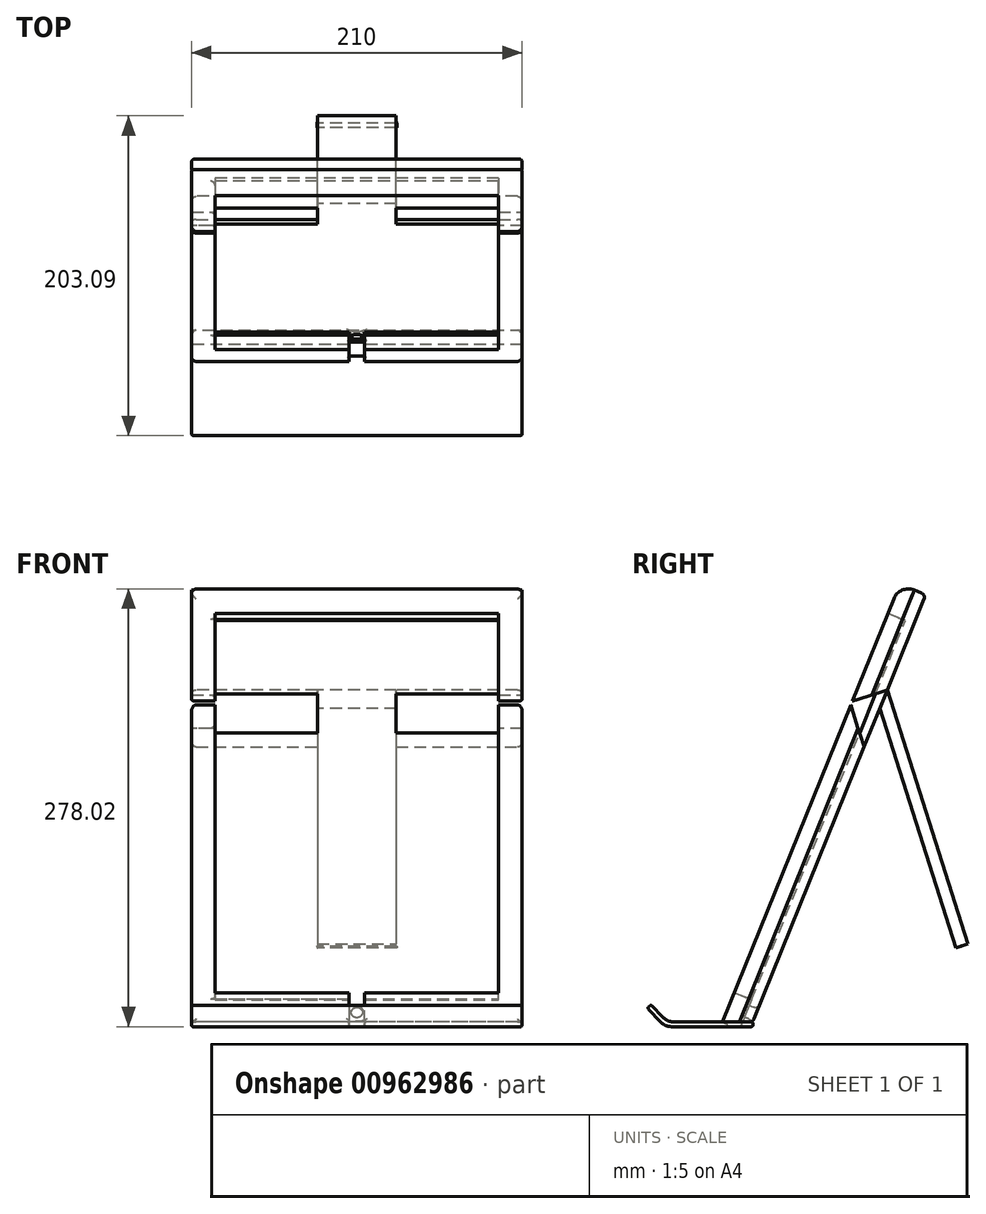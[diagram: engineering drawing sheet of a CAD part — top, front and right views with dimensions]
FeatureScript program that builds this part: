
annotation { "Feature Type Name" : "Feature", "Feature Type Description" : "" }
export const myFeature = defineFeature(function(context is Context, id is Id, definition is map)
    precondition{}
    {
        {
            var Q0;
            Q0=qCreatedBy(makeId("Right.planeOp"),FACE);
            var sketch = newSketch(context, id + "F0", { "sketchPlane" : qUnion([Q0])});
            skLineSegment(sketch, "E0", {"start": v(10.79, 0) * mm, "end": v(121.93, 274.29) * mm});
            skLineSegment(sketch, "E1", {"start": v(121.93, 274.29) * mm, "end": v(112.66, 278.04) * mm});
            skLineSegment(sketch, "E2", {"start": v(112.66, 278.04) * mm, "end": v(0, 0) * mm});
            skLineSegment(sketch, "E3", {"start": v(0, 0) * mm, "end": v(10.79, 0) * mm});
            skSolve(sketch);
        }
        {
            var Q0;
            Q0 = qSketchRegion(id + "F0", true);
            extrude(context, id + "F1", {"entities" : qUnion([Q0]), "depth" : 210 * mm, "offsetDistance" : 25 * mm});
        }
        {
            var Q0;
            Q0=qCreatedBy(makeId("Right.planeOp"),FACE);
            var sketch = newSketch(context, id + "F2", { "sketchPlane" : qUnion([Q0])});
            skLineSegment(sketch, "E4.0", {"start": v(10.79, 0) * mm, "end": v(121.93, 274.29) * mm});
            skLineSegment(sketch, "E5", {"start": v(121.93, 274.29) * mm, "end": v(129.34, 271.28) * mm});
            skLineSegment(sketch, "E6", {"start": v(129.34, 271.28) * mm, "end": v(19.42, 0) * mm});
            skLineSegment(sketch, "E7", {"start": v(19.42, 0) * mm, "end": v(10.79, 0) * mm});
            skSolve(sketch);
        }
        {
            var Q0;
            Q0 = qSketchRegion(id + "F2", true);
            extrude(context, id + "F3", {"entities" : qUnion([Q0]), "depth" : 210 * mm, "offsetDistance" : 25 * mm});
        }
        {
            var Q0;
            Q0=makeQuery(id+"F1.opExtrude","SWEPT_EDGE",EDGE,{"disambiguationData":[OSD([sQuery(id+"F0.wireOp",EDGE,"E1"),sQuery(id+"F0.wireOp",EDGE,"E2")])]});
            fillet(context, id + "F4", {"entities" : qUnion([Q0]), "radius" : 10 * mm, "tangentPropagation" : true, "allowEdgeOverflow" : false});
        }
        {
            var Q0;
            Q0=qCreatedBy(makeId("Right.planeOp"),FACE);
            var sketch = newSketch(context, id + "F5", { "sketchPlane" : qUnion([Q0])});
            skLineSegment(sketch, "E8.0", {"start": v(0, 0) * mm, "end": v(10.79, 0) * mm});
            skLineSegment(sketch, "E9.0", {"start": v(19.42, 0) * mm, "end": v(10.79, 0) * mm});
            skLineSegment(sketch, "E10", {"start": v(19.42, 0) * mm, "end": v(19.42, -3) * mm});
            skLineSegment(sketch, "E11", {"start": v(0, 0) * mm, "end": v(-35, 0) * mm});
            skLineSegment(sketch, "E12", {"start": v(-35, 0) * mm, "end": v(-45.29, 10.92) * mm});
            skLineSegment(sketch, "E13", {"start": v(-45.29, 10.92) * mm, "end": v(-47.47, 8.86) * mm});
            skLineSegment(sketch, "E14", {"start": v(-47.47, 8.86) * mm, "end": v(-36.3, -3) * mm});
            skLineSegment(sketch, "E15", {"start": v(19.42, -3) * mm, "end": v(-36.3, -3) * mm});
            skSolve(sketch);
        }
        {
            var Q0;
            Q0=makeQuery(id+"F1.opExtrude","SWEPT_FACE",FACE,{"disambiguationData":[OSD([sQuery(id+"F0.wireOp",EDGE,"E2")])]});
            var sketch = newSketch(context, id + "F6", { "sketchPlane" : qUnion([Q0])});
            skLineSegment(sketch, "E16", {"start": v(15, 20) * mm, "end": v(100, 20) * mm});
            skLineSegment(sketch, "E17", {"start": v(195, 20) * mm, "end": v(195, 280) * mm});
            skLineSegment(sketch, "E18", {"start": v(195, 280) * mm, "end": v(15, 280) * mm});
            skLineSegment(sketch, "E19", {"start": v(15, 280) * mm, "end": v(15, 20) * mm});
            skLineSegment(sketch, "E20", {"start": v(105, 0) * mm, "end": v(110, 0) * mm});
            skLineSegment(sketch, "E21", {"start": v(110, 0) * mm, "end": v(110, 20) * mm});
            skLineSegment(sketch, "E22", {"start": v(100, 20) * mm, "end": v(100, 0) * mm});
            skLineSegment(sketch, "E23", {"start": v(100, 0) * mm, "end": v(105, 0) * mm});
            skLineSegment(sketch, "E24.trimOffspring", {"start": v(110, 20) * mm, "end": v(195, 20) * mm});
            skSolve(sketch);
        }
        {
            var Q0;
            Q0 = qSketchRegion(id + "F5", true);
            extrude(context, id + "F7", {"entities" : qUnion([Q0]), "depth" : 210 * mm, "offsetDistance" : 25 * mm});
        }
        {
            var Q0;
            Q0 = qSketchRegion(id + "F6", true);
            extrude(context, id + "F8", {"entities" : qUnion([Q0]), "operationType" : NewBodyOperationType.REMOVE, "oppositeDirection" : true, "depth" : 12 * mm, "offsetDistance" : 25 * mm});
        }
        {
            var Q0;
            Q0=makeQuery(id+"F3.opExtrude","SWEPT_FACE",FACE,{"disambiguationData":[OSD([sQuery(id+"F2.wireOp",EDGE,"E4.0")])]});
            var sketch = newSketch(context, id + "F9", { "sketchPlane" : qUnion([Q0])});
            skCircle(sketch, "E25", {"center": v(105, 12.05) * mm, "radius": 4 * mm});
            skLineSegment(sketch, "E26", {"start": v(105, 4.05) * mm, "end": v(105, 12.05) * mm, "construction": true});
            skSolve(sketch);
        }
        {
            var Q0;
            Q0 = qSketchRegion(id + "F9", true);
            extrude(context, id + "F10", {"entities" : qUnion([Q0]), "operationType" : NewBodyOperationType.REMOVE, "oppositeDirection" : true, "depth" : 25 * mm, "offsetDistance" : 25 * mm});
        }
        {
            var Q0;
            Q0=makeQuery(id+"F1.opExtrude","CAP_EDGE",EDGE,{"disambiguationData":[OSD([sQuery(id+"F0.wireOp",EDGE,"E2")])],"isStart":false});
            var Q1;
            Q1=makeQuery(id+"F1.opExtrude","CAP_EDGE",EDGE,{"disambiguationData":[OSD([sQuery(id+"F0.wireOp",EDGE,"E2")])],"isStart":true});
            var Q2;
            Q2=makeQuery(id+"F3.opExtrude","SWEPT_FACE",FACE,{"disambiguationData":[OSD([sQuery(id+"F2.wireOp",EDGE,"E6")])]});
            var Q3;
            Q3=makeQuery(id+"F8.boolean.opBoolean","COPY",EDGE,{"derivedFrom":makeQuery(id+"F8.opExtrude","CAP_EDGE",EDGE,{"disambiguationData":[OSD([sQuery(id+"F6.wireOp",EDGE,"E16")])],"isStart":true})});
            var Q4;
            Q4=makeQuery(id+"F8.boolean.opBoolean","INTERSECT",EDGE,{"derivedFrom":[makeQuery(id+"F1.opExtrude","SWEPT_FACE",FACE,{"disambiguationData":[OSD([sQuery(id+"F0.wireOp",EDGE,"E0")])]}),makeQuery(id+"F8.opExtrude","SWEPT_FACE",FACE,{"disambiguationData":[OSD([sQuery(id+"F6.wireOp",EDGE,"E19")])]})]});
            var Q5;
            Q5=makeQuery(id+"F8.boolean.opBoolean","COPY",EDGE,{"derivedFrom":makeQuery(id+"F8.opExtrude","CAP_EDGE",EDGE,{"disambiguationData":[OSD([sQuery(id+"F6.wireOp",EDGE,"E17")])],"isStart":true})});
            var Q6;
            Q6=makeQuery(id+"F8.boolean.opBoolean","COPY",EDGE,{"derivedFrom":makeQuery(id+"F8.opExtrude","CAP_EDGE",EDGE,{"disambiguationData":[OSD([sQuery(id+"F6.wireOp",EDGE,"E24.trimOffspring")])],"isStart":true})});
            var Q7;
            Q7=makeQuery(id+"F8.boolean.opBoolean","COPY",EDGE,{"derivedFrom":makeQuery(id+"F8.opExtrude","CAP_EDGE",EDGE,{"disambiguationData":[OSD([sQuery(id+"F6.wireOp",EDGE,"E19")])],"isStart":true})});
            var Q8;
            Q8=makeQuery(id+"F8.boolean.opBoolean","COPY",EDGE,{"derivedFrom":makeQuery(id+"F8.opExtrude","CAP_EDGE",EDGE,{"disambiguationData":[OSD([sQuery(id+"F6.wireOp",EDGE,"E21")])],"isStart":true})});
            var Q9;
            Q9=makeQuery(id+"F8.boolean.opBoolean","COPY",EDGE,{"derivedFrom":makeQuery(id+"F8.opExtrude","CAP_EDGE",EDGE,{"disambiguationData":[OSD([sQuery(id+"F6.wireOp",EDGE,"E22")])],"isStart":true})});
            var Q10;
            Q10=makeQuery(id+"F8.boolean.opBoolean","COPY",EDGE,{"derivedFrom":makeQuery(id+"F8.opExtrude","CAP_EDGE",EDGE,{"disambiguationData":[OSD([sQuery(id+"F6.wireOp",EDGE,"E18")])],"isStart":true})});
            fillet(context, id + "F11", {"entities" : qUnion([Q0, Q1, Q2, Q3, Q4, Q5, Q6, Q7, Q8, Q9, Q10]), "radius" : 3 * mm, "tangentPropagation" : true, "allowEdgeOverflow" : false});
        }
        {
            var Q0;
            Q0=qCreatedBy(makeId("Right.planeOp"),FACE);
            var sketch = newSketch(context, id + "F12", { "sketchPlane" : qUnion([Q0])});
            skLineSegment(sketch, "E27.0", {"start": v(128.22, 268.5) * mm, "end": v(20.18, 1.87) * mm});
            skLineSegment(sketch, "E28", {"start": v(100.14, 199.2) * mm, "end": v(163.38, 0) * mm});
            skLineSegment(sketch, "E29", {"start": v(163.38, 0) * mm, "end": v(171, 2.42) * mm});
            skLineSegment(sketch, "E30", {"start": v(171, 2.42) * mm, "end": v(104.84, 210.82) * mm});
            skSolve(sketch);
        }
        {
            var Q0;
            Q0 = qSketchRegion(id + "F12", true);
            extrude(context, id + "F13", {"entities" : qUnion([Q0]), "depth" : 210 * mm, "offsetDistance" : 25 * mm});
        }
        {
            var Q0;
            Q0=makeQuery(id+"F13.opExtrude","SWEPT_FACE",FACE,{"disambiguationData":[OSD([sQuery(id+"F12.wireOp",EDGE,"E30")])]});
            var sketch = newSketch(context, id + "F14", { "sketchPlane" : qUnion([Q0])});
            skLineSegment(sketch, "E31", {"start": v(-105, -49.44) * mm, "end": v(-105, 239.2) * mm, "construction": true});
            skLineSegment(sketch, "E32", {"start": v(-190, -20) * mm, "end": v(-210, -49.44) * mm});
            skLineSegment(sketch, "E33", {"start": v(-20, -20) * mm, "end": v(0, -49.44) * mm});
            skPoint(sketch, "E34.orphan", {"position": v(0, -19.85) * mm});
            skLineSegment(sketch, "E35", {"start": v(-210, -49.44) * mm, "end": v(-210, 169.2) * mm});
            skLineSegment(sketch, "E36", {"start": v(-210, 169.2) * mm, "end": v(-130, 169.2) * mm});
            skLineSegment(sketch, "E37", {"start": v(-80, 169.2) * mm, "end": v(0, 169.2) * mm});
            skLineSegment(sketch, "E38", {"start": v(0, 169.2) * mm, "end": v(0, -49.44) * mm});
            skLineSegment(sketch, "E39", {"start": v(0, -49.44) * mm, "end": v(-20, -20) * mm});
            skPoint(sketch, "E40.start.orphan", {"position": v(-105, 169.2) * mm});
            skPoint(sketch, "E41.end.orphan", {"position": v(-130, 0) * mm});
            skPoint(sketch, "E42.end.orphan", {"position": v(-80.13, 0) * mm});
            skLineSegment(sketch, "E43", {"start": v(-80, 169.2) * mm, "end": v(-80, -0.8) * mm});
            skLineSegment(sketch, "E44", {"start": v(-80, -0.8) * mm, "end": v(-80, 169.2) * mm});
            skLineSegment(sketch, "E45", {"start": v(-130, 169.2) * mm, "end": v(-130, -0.8) * mm});
            skLineSegment(sketch, "E46", {"start": v(-80, -0.8) * mm, "end": v(-20, -20) * mm});
            skLineSegment(sketch, "E47", {"start": v(-20, -20) * mm, "end": v(0, -20) * mm});
            skLineSegment(sketch, "E48", {"start": v(-130, 169.2) * mm, "end": v(-80, 169.2) * mm});
            skLineSegment(sketch, "E49", {"start": v(-190, -20) * mm, "end": v(-210, -20) * mm});
            skLineSegment(sketch, "E50", {"start": v(-130, -0.8) * mm, "end": v(-190, -20) * mm});
            skSolve(sketch);
        }
        {
            var Q0;
            Q0 = qSketchRegion(id + "F14", true);
            extrude(context, id + "F15", {"entities" : qUnion([Q0]), "operationType" : NewBodyOperationType.REMOVE, "oppositeDirection" : true, "depth" : 25 * mm, "offsetDistance" : 25 * mm});
        }
        {
            var Q0;
            Q0=makeQuery(id+"F15.boolean.opBoolean","COPY",EDGE,{"derivedFrom":makeQuery(id+"F15.opExtrude","CAP_EDGE",EDGE,{"disambiguationData":[OSD([sQuery(id+"F14.wireOp",EDGE,"E42")])],"isStart":true})});
            var Q1;
            Q1=makeQuery(id+"F15.boolean.opBoolean","COPY",EDGE,{"derivedFrom":makeQuery(id+"F15.opExtrude","CAP_EDGE",EDGE,{"disambiguationData":[OSD([sQuery(id+"F14.wireOp",EDGE,"E41")])],"isStart":true})});
            var Q2;
            Q2=makeQuery(id+"F15.boolean.opBoolean","COPY",EDGE,{"derivedFrom":makeQuery(id+"F15.opExtrude","CAP_EDGE",EDGE,{"disambiguationData":[OSD([sQuery(id+"F14.wireOp",EDGE,"zWq83p2V-2280-gHE3-ipJg-bSoWOM0zsTTD")])],"isStart":true})});
            var Q3;
            Q3=makeQuery(id+"F15.boolean.opBoolean","COPY",EDGE,{"derivedFrom":makeQuery(id+"F15.opExtrude","CAP_EDGE",EDGE,{"disambiguationData":[OSD([sQuery(id+"F14.wireOp",EDGE,"E32")])],"isStart":true})});
            var Q4;
            Q4=makeQuery(id+"F13.opExtrude","SWEPT_EDGE",EDGE,{"disambiguationData":[OSD([sQuery(id+"F12.wireOp",EDGE,"E29"),sQuery(id+"F12.wireOp",EDGE,"E30")])]});
            var Q5;
            Q5=makeQuery(id+"F15.boolean.opBoolean","COPY",EDGE,{"derivedFrom":makeQuery(id+"F15.opExtrude","CAP_EDGE",EDGE,{"disambiguationData":[OSD([sQuery(id+"F14.wireOp",EDGE,"E39")])],"isStart":true})});
            var Q6;
            Q6=makeQuery(id+"F15.boolean.opBoolean","COPY",EDGE,{"derivedFrom":makeQuery(id+"F15.opExtrude","CAP_EDGE",EDGE,{"disambiguationData":[OSD([sQuery(id+"F14.wireOp",EDGE,"iIxzz1AC-Ownc-jVEO-BnMf-pMrgPYKgyDFp")])],"isStart":true})});
            var Q7;
            Q7=makeQuery(id+"F15.boolean.opBoolean","COPY",EDGE,{"derivedFrom":makeQuery(id+"F15.opExtrude","CAP_EDGE",EDGE,{"disambiguationData":[OSD([sQuery(id+"F14.wireOp",EDGE,"E50")])],"isStart":true})});
            var Q8;
            Q8=makeQuery(id+"F15.boolean.opBoolean","COPY",EDGE,{"derivedFrom":makeQuery(id+"F15.opExtrude","CAP_EDGE",EDGE,{"disambiguationData":[OSD([sQuery(id+"F14.wireOp",EDGE,"E46")])],"isStart":true})});
            var Q9;
            Q9=makeQuery(id+"F15.boolean.opBoolean","COPY",EDGE,{"derivedFrom":makeQuery(id+"F15.opExtrude","CAP_EDGE",EDGE,{"disambiguationData":[OSD([sQuery(id+"F14.wireOp",EDGE,"E44")])],"isStart":true})});
            var Q10;
            Q10=makeQuery(id+"F15.boolean.opBoolean","COPY",EDGE,{"derivedFrom":makeQuery(id+"F15.opExtrude","CAP_EDGE",EDGE,{"disambiguationData":[OSD([sQuery(id+"F14.wireOp",EDGE,"E45")])],"isStart":true})});
            fillet(context, id + "F16", {"entities" : qUnion([Q0, Q1, Q2, Q3, Q4, Q5, Q6, Q7, Q8, Q9, Q10]), "radius" : 5 * mm, "tangentPropagation" : true, "allowEdgeOverflow" : false});
        }
        {
            var Q0;
            Q0=makeQuery(id+"F7.opExtrude","SWEPT_EDGE",EDGE,{"disambiguationData":[OSD([sQuery(id+"F5.wireOp",EDGE,"E11"),sQuery(id+"F5.wireOp",EDGE,"E12")])]});
            var Q1;
            Q1=makeQuery(id+"F7.opExtrude","SWEPT_EDGE",EDGE,{"disambiguationData":[OSD([sQuery(id+"F5.wireOp",EDGE,"E14"),sQuery(id+"F5.wireOp",EDGE,"E15")])]});
            fillet(context, id + "F17", {"entities" : qUnion([Q0, Q1]), "radius" : 10 * mm, "tangentPropagation" : true, "allowEdgeOverflow" : false});
        }
        {
            var Q0;
            Q0=makeQuery(id+"F7.opExtrude","SWEPT_FACE",FACE,{"disambiguationData":[OSD([sQuery(id+"F5.wireOp",EDGE,"E8.0"),sQuery(id+"F5.wireOp",EDGE,"E9.0"),sQuery(id+"F5.wireOp",EDGE,"E11")])]});
            var Q1;
            Q1=makeQuery(id+"F7.opExtrude","SWEPT_FACE",FACE,{"disambiguationData":[OSD([sQuery(id+"F5.wireOp",EDGE,"E15")])]});
            var Q2;
            Q2=makeQuery(id+"F7.opExtrude","SWEPT_FACE",FACE,{"disambiguationData":[OSD([sQuery(id+"F5.wireOp",EDGE,"E13")])]});
            fillet(context, id + "F18", {"entities" : qUnion([Q0, Q1, Q2]), "radius" : 1 * mm, "tangentPropagation" : true, "allowEdgeOverflow" : false});
        }
        {
            var Q0;
            Q0=makeQuery(id+"F13.opExtrude","SWEPT_FACE",FACE,{"disambiguationData":[OSD([sQuery(id+"F12.wireOp",EDGE,"E30")])]});
            var sketch = newSketch(context, id + "F19", { "sketchPlane" : qUnion([Q0])});
            skLineSegment(sketch, "E51.0", {"start": v(0, -49.44) * mm, "end": v(-210, -49.44) * mm});
            skLineSegment(sketch, "E52", {"start": v(-210, -49.44) * mm, "end": v(-193.05, -16.8) * mm});
            skLineSegment(sketch, "E53", {"start": v(-193.05, -16.8) * mm, "end": v(-130.1, 0) * mm});
            skLineSegment(sketch, "E54", {"start": v(-105, -49.44) * mm, "end": v(-105, -14.89) * mm, "construction": true});
            skLineSegment(sketch, "E55.MirrorCS", {"start": v(-16.95, -16.8) * mm, "end": v(-79.9, 0) * mm});
            skLineSegment(sketch, "E56.MirrorCS", {"start": v(0, -49.44) * mm, "end": v(-16.95, -16.8) * mm});
            skLineSegment(sketch, "E57", {"start": v(-130.1, 0) * mm, "end": v(-79.9, 0) * mm});
            skPoint(sketch, "E58.MirrorCS.start.orphan", {"position": v(-79.9, 0) * mm});
            skSolve(sketch);
        }
        {
            var Q0;
            Q0 = qSketchRegion(id + "F19", true);
            extrude(context, id + "F20", {"entities" : qUnion([Q0]), "oppositeDirection" : true, "depth" : 8 * mm, "offsetDistance" : 25 * mm});
        }
        {
            var Q0;
            Q0=makeQuery(id+"F20.opExtrude","SWEPT_FACE",FACE,{"disambiguationData":[OSD([sQuery(id+"F19.wireOp",EDGE,"E51.0")])]});
            var sketch = newSketch(context, id + "F21", { "sketchPlane" : qUnion([Q0])});
            skPoint(sketch, "E59.0.start.orphan", {"position": v(130, -158.72) * mm});
            skPoint(sketch, "E60.0.end.orphan", {"position": v(80, -158.72) * mm});
            skLineSegment(sketch, "E61", {"start": v(130, -158.72) * mm, "end": v(130, -163.72) * mm});
            skLineSegment(sketch, "E62", {"start": v(130, -163.72) * mm, "end": v(80, -163.72) * mm});
            skLineSegment(sketch, "E63", {"start": v(80, -163.72) * mm, "end": v(80, -158.72) * mm});
            skLineSegment(sketch, "E64", {"start": v(130, -158.72) * mm, "end": v(80, -158.72) * mm});
            skSolve(sketch);
        }
        {
            var Q0;
            Q0 = qSketchRegion(id + "F21", true);
            extrude(context, id + "F22", {"entities" : qUnion([Q0]), "operationType" : NewBodyOperationType.REMOVE, "oppositeDirection" : true, "depth" : 49.48 * mm, "offsetDistance" : 25 * mm});
        }
        {
            var Q0;
            Q0=makeQuery(id+"F13.opExtrude","SWEPT_FACE",FACE,{"disambiguationData":[OSD([sQuery(id+"F12.wireOp",EDGE,"E29")])]});
            var sketch = newSketch(context, id + "F23", { "sketchPlane" : qUnion([Q0])});
            skLineSegment(sketch, "E65", {"start": v(130, -158.72) * mm, "end": v(130, -164.65) * mm});
            skLineSegment(sketch, "E66", {"start": v(130, -164.65) * mm, "end": v(215.08, -164.65) * mm});
            skLineSegment(sketch, "E67", {"start": v(215.08, -164.65) * mm, "end": v(215.08, -152.09) * mm});
            skLineSegment(sketch, "E68", {"start": v(215.08, -152.09) * mm, "end": v(-9, -152.09) * mm});
            skLineSegment(sketch, "E69", {"start": v(-9, -152.09) * mm, "end": v(-9, -168.07) * mm});
            skLineSegment(sketch, "E70", {"start": v(-9, -168.07) * mm, "end": v(80, -168.07) * mm});
            skLineSegment(sketch, "E71", {"start": v(80, -168.07) * mm, "end": v(80, -158.72) * mm});
            skLineSegment(sketch, "E72", {"start": v(130, -158.72) * mm, "end": v(80, -158.72) * mm});
            skPoint(sketch, "E73.0.start.orphan", {"position": v(80, -155.72) * mm});
            skPoint(sketch, "E74.0.end.orphan", {"position": v(130, -155.72) * mm});
            skSolve(sketch);
        }
        {
            var Q0;
            Q0 = qSketchRegion(id + "F23", true);
            extrude(context, id + "F24", {"entities" : qUnion([Q0]), "operationType" : NewBodyOperationType.REMOVE, "oppositeDirection" : true, "depth" : 49.37 * mm, "offsetDistance" : 25 * mm});
        }
        {
            var Q0;
            {var subQ0=sQuery(id+"F19.wireOp",EDGE,"E51.0");var subQ1=sQuery(id+"F19.wireOp",EDGE,"E56.MirrorCS");Q0=makeQuery(id+"F22.boolean.opBoolean","SPLIT",EDGE,{"disambiguationData":[TD([makeQuery(id+"F20.opExtrude","SWEPT_FACE",FACE,{"disambiguationData":[OSD([subQ1])]})])],"derivedFrom":makeQuery(id+"F20.opExtrude","CAP_EDGE",EDGE,{"disambiguationData":[OSD([subQ0])],"isStart":true})});}
            var Q1;
            Q1=makeQuery(id+"F20.opExtrude","CAP_EDGE",EDGE,{"disambiguationData":[OSD([sQuery(id+"F19.wireOp",EDGE,"E55.MirrorCS")])],"isStart":true});
            var Q2;
            Q2=makeQuery(id+"F20.opExtrude","CAP_EDGE",EDGE,{"disambiguationData":[OSD([sQuery(id+"F19.wireOp",EDGE,"E56.MirrorCS")])],"isStart":true});
            var Q3;
            {var subQ0=sQuery(id+"F19.wireOp",EDGE,"E51.0");var subQ1=sQuery(id+"F19.wireOp",EDGE,"E52");Q3=makeQuery(id+"F22.boolean.opBoolean","SPLIT",EDGE,{"disambiguationData":[TD([makeQuery(id+"F20.opExtrude","SWEPT_FACE",FACE,{"disambiguationData":[OSD([subQ1])]})])],"derivedFrom":makeQuery(id+"F20.opExtrude","CAP_EDGE",EDGE,{"disambiguationData":[OSD([subQ0])],"isStart":true})});}
            var Q4;
            Q4=makeQuery(id+"F20.opExtrude","CAP_EDGE",EDGE,{"disambiguationData":[OSD([sQuery(id+"F19.wireOp",EDGE,"E53")])],"isStart":true});
            var Q5;
            Q5=makeQuery(id+"F20.opExtrude","CAP_EDGE",EDGE,{"disambiguationData":[OSD([sQuery(id+"F19.wireOp",EDGE,"E52")])],"isStart":true});
            fillet(context, id + "F25", {"entities" : qUnion([Q0, Q1, Q2, Q3, Q4, Q5]), "radius" : 5 * mm, "tangentPropagation" : true, "allowEdgeOverflow" : false});
        }
    });
